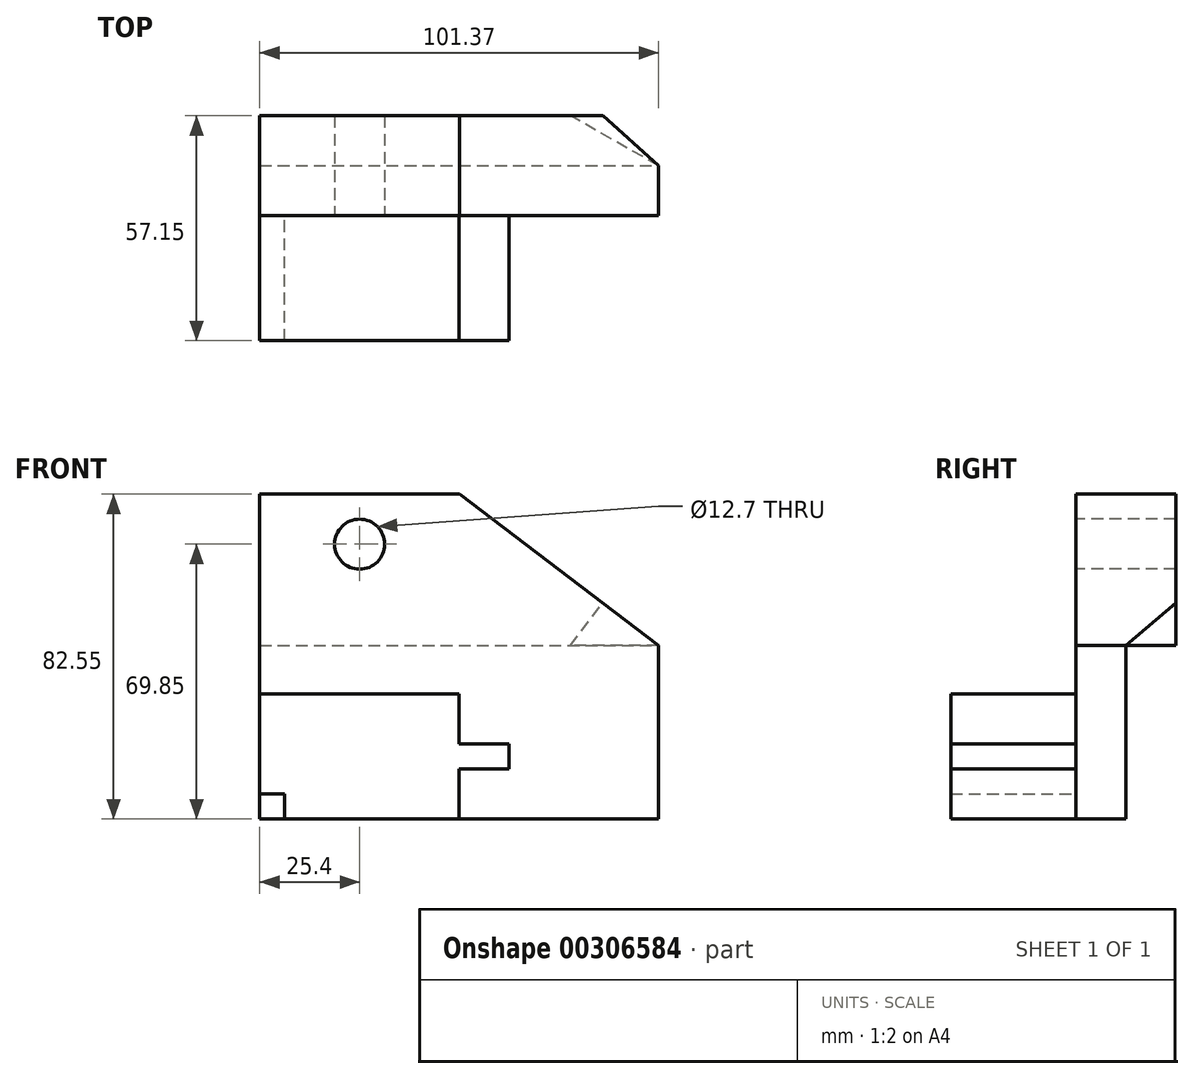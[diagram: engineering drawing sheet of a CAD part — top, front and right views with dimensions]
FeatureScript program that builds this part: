
annotation { "Feature Type Name" : "Feature", "Feature Type Description" : "" }
export const myFeature = defineFeature(function(context is Context, id is Id, definition is map)
    precondition{}
    {
        {
            var Q0;
            Q0=qCreatedBy(makeId("Front.planeOp"),FACE);
            var sketch = newSketch(context, id + "F0", { "sketchPlane" : qUnion([Q0])});
            skLineSegment(sketch, "E0", {"start": v(0, 0) * mm, "end": v(0, 82.55) * mm});
            skLineSegment(sketch, "E1", {"start": v(0, 82.55) * mm, "end": v(50.8, 82.55) * mm});
            skLineSegment(sketch, "E2", {"start": v(50.8, 82.55) * mm, "end": v(101.37, 44.15) * mm});
            skLineSegment(sketch, "E3", {"start": v(101.37, 0) * mm, "end": v(0, 0) * mm});
            skLineSegment(sketch, "E4", {"start": v(101.37, 44.15) * mm, "end": v(101.37, 0) * mm});
            skSolve(sketch);
        }
        {
            var Q0;
            Q0 = qSketchRegion(id + "F0", true);
            extrude(context, id + "F1", {"entities" : qUnion([Q0]), "depth" : 25.4 * mm});
        }
        {
            var Q0;
            Q0=makeQuery(id+"F1.opExtrude","SWEPT_FACE",FACE,{"disambiguationData":[OSD([sQuery(id+"F0.wireOp",EDGE,"E2")])]});
            var sketch = newSketch(context, id + "F2", { "sketchPlane" : qUnion([Q0])});
            skLineSegment(sketch, "E5", {"start": v(54.03, -12.7) * mm, "end": v(36.2, 0) * mm});
            skSolve(sketch);
        }
        {
            var Q0;
            {var subQ0=sQuery(id+"F2.wireOp",EDGE,"E5");Q0=makeQuery(id+"F2.imprint","IMPRINT",FACE,{"disambiguationData":[TD([[makeQuery(id+"F2.imprint","IMPRINT",EDGE,{"derivedFrom":subQ0}),-1.0]])]});}
            extrude(context, id + "F3", {"entities" : qUnion([Q0]), "operationType" : NewBodyOperationType.REMOVE, "endBound" : BoundingType.THROUGH_ALL, "oppositeDirection" : true, "depth" : 25.4 * mm});
        }
        {
            var Q0;
            Q0=makeQuery(id+"F1.opExtrude","SWEPT_FACE",FACE,{"disambiguationData":[OSD([sQuery(id+"F0.wireOp",EDGE,"E4")])]});
            var sketch = newSketch(context, id + "F4", { "sketchPlane" : qUnion([Q0])});
            skLineSegment(sketch, "E6.bottom", {"start": v(-25.4, 44.15) * mm, "end": v(-12.7, 44.15) * mm});
            skLineSegment(sketch, "E6.top", {"start": v(-25.4, 0) * mm, "end": v(-12.7, 0) * mm});
            skLineSegment(sketch, "E6.left", {"start": v(-25.4, 44.15) * mm, "end": v(-25.4, 0) * mm});
            skLineSegment(sketch, "E6.right", {"start": v(-12.7, 44.15) * mm, "end": v(-12.7, 0) * mm});
            skSolve(sketch);
        }
        {
            var Q0;
            {var subQ0=sQuery(id+"F4.wireOp",EDGE,"E6.right");Q0=makeQuery(id+"F4.imprint","IMPRINT",FACE,{"disambiguationData":[TD([[makeQuery(id+"F4.imprint","IMPRINT",EDGE,{"derivedFrom":subQ0}),1.0]])]});}
            extrude(context, id + "F5", {"entities" : qUnion([Q0]), "operationType" : NewBodyOperationType.REMOVE, "endBound" : BoundingType.THROUGH_ALL, "oppositeDirection" : true, "depth" : 25.4 * mm});
        }
        {
            var Q0;
            Q0=makeQuery(id+"F1.opExtrude","CAP_FACE",FACE,{"disambiguationData":[OSD([sQuery(id+"F0.wireOp",EDGE,"E0"),sQuery(id+"F0.wireOp",EDGE,"E1"),sQuery(id+"F0.wireOp",EDGE,"E2"),sQuery(id+"F0.wireOp",EDGE,"E3"),sQuery(id+"F0.wireOp",EDGE,"E4")])],"isStart":false});
            var sketch = newSketch(context, id + "F6", { "sketchPlane" : qUnion([Q0])});
            skCircle(sketch, "E7", {"center": v(25.4, 69.85) * mm, "radius": 6.35 * mm});
            skSolve(sketch);
        }
        {
            var Q0;
            Q0=makeQuery(id+"F6.imprint","IMPRINT",FACE,{"disambiguationData":[TD([[makeQuery(id+"F6.imprint","IMPRINT",EDGE,{"derivedFrom":sQuery(id+"F6.wireOp",EDGE,"E7")}),1.0]])]});
            extrude(context, id + "F7", {"entities" : qUnion([Q0]), "operationType" : NewBodyOperationType.REMOVE, "endBound" : BoundingType.THROUGH_ALL, "oppositeDirection" : true, "depth" : 25.4 * mm});
        }
        {
            var Q0;
            Q0=makeQuery(id+"F1.opExtrude","CAP_FACE",FACE,{"disambiguationData":[OSD([sQuery(id+"F0.wireOp",EDGE,"E0"),sQuery(id+"F0.wireOp",EDGE,"E1"),sQuery(id+"F0.wireOp",EDGE,"E2"),sQuery(id+"F0.wireOp",EDGE,"E3"),sQuery(id+"F0.wireOp",EDGE,"E4")])],"isStart":false});
            var sketch = newSketch(context, id + "F8", { "sketchPlane" : qUnion([Q0])});
            skLineSegment(sketch, "E8", {"start": v(0, 31.75) * mm, "end": v(0, 6.35) * mm});
            skLineSegment(sketch, "E9", {"start": v(0, 6.35) * mm, "end": v(6.35, 6.35) * mm});
            skLineSegment(sketch, "E10", {"start": v(6.35, 6.35) * mm, "end": v(6.35, 0) * mm});
            skLineSegment(sketch, "E11", {"start": v(6.35, 0) * mm, "end": v(50.69, 0) * mm});
            skLineSegment(sketch, "E12", {"start": v(50.69, 0) * mm, "end": v(50.69, 12.7) * mm});
            skLineSegment(sketch, "E13", {"start": v(50.69, 12.7) * mm, "end": v(63.39, 12.7) * mm});
            skLineSegment(sketch, "E14", {"start": v(63.39, 12.7) * mm, "end": v(63.39, 19.05) * mm});
            skLineSegment(sketch, "E15", {"start": v(63.39, 19.05) * mm, "end": v(50.69, 19.05) * mm});
            skLineSegment(sketch, "E16", {"start": v(50.69, 19.05) * mm, "end": v(50.69, 31.75) * mm});
            skLineSegment(sketch, "E17", {"start": v(50.69, 31.75) * mm, "end": v(0, 31.75) * mm});
            skSolve(sketch);
        }
        {
            var Q0;
            Q0=makeQuery(id+"F8.imprint","IMPRINT",FACE,{"disambiguationData":[TD([[makeQuery(id+"F8.imprint","IMPRINT",EDGE,{"derivedFrom":sQuery(id+"F8.wireOp",EDGE,"E8")}),-1.0]])]});
            extrude(context, id + "F9", {"entities" : qUnion([Q0]), "operationType" : NewBodyOperationType.ADD, "depth" : 31.75 * mm});
        }
    });
